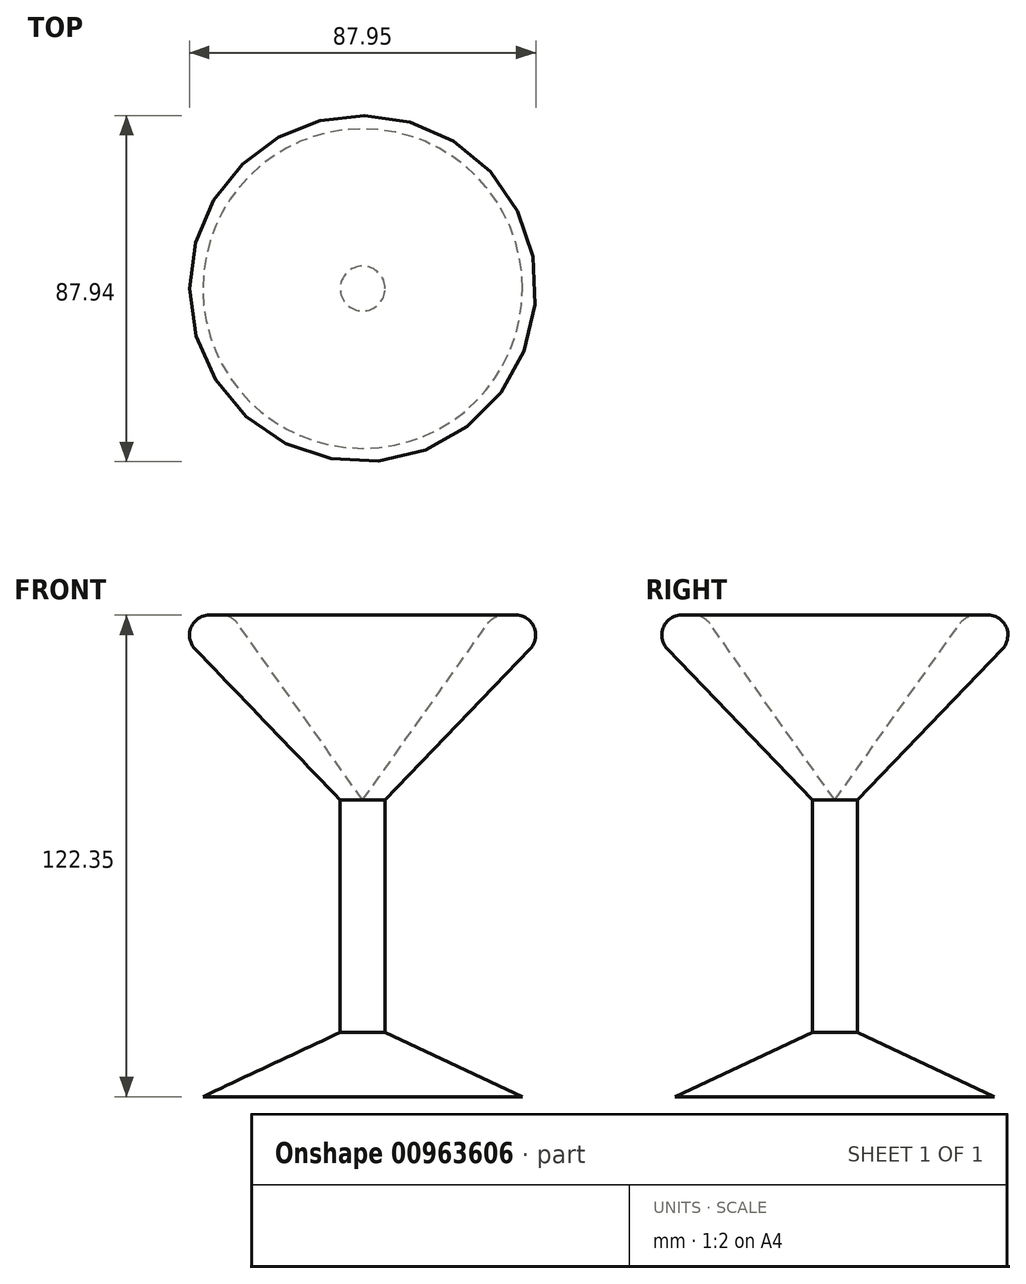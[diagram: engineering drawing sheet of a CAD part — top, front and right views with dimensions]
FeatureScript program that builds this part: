
annotation { "Feature Type Name" : "Feature", "Feature Type Description" : "" }
export const myFeature = defineFeature(function(context is Context, id is Id, definition is map)
    precondition{}
    {
        {
            var Q0;
            Q0=qCreatedBy(makeId("Front.planeOp"),FACE);
            var sketch = newSketch(context, id + "F0", { "sketchPlane" : qUnion([Q0])});
            skLineSegment(sketch, "E0", {"start": v(27.6, 56.5) * mm, "end": v(45.12, 56.5) * mm});
            skLineSegment(sketch, "E1", {"start": v(45.12, 56.5) * mm, "end": v(0, 9.5) * mm});
            skLineSegment(sketch, "E2", {"start": v(0, 9.5) * mm, "end": v(0, -49.5) * mm});
            skLineSegment(sketch, "E3", {"start": v(0, -49.5) * mm, "end": v(34.9, -65.85) * mm});
            skLineSegment(sketch, "E4", {"start": v(34.9, -65.85) * mm, "end": v(-5.7, -65.85) * mm});
            skLineSegment(sketch, "E5", {"start": v(-5.7, -65.85) * mm, "end": v(-5.7, 9.5) * mm});
            skLineSegment(sketch, "E6", {"start": v(-5.7, 9.5) * mm, "end": v(27.6, 56.5) * mm});
            skSolve(sketch);
        }
        {
            var Q0;
            Q0=makeQuery(id+"F0.imprint","IMPRINT",FACE,{"disambiguationData":[TD([[makeQuery(id+"F0.imprint","IMPRINT",EDGE,{"derivedFrom":sQuery(id+"F0.wireOp",EDGE,"E0")}),-1.0]])]});
            var Q1;
            Q1=sQuery(id+"F0.wireOp",EDGE,"E5");
            revolve(context, id + "F1", {"surfaceOperationType" : NewSurfaceOperationType.NEW, "entities" : qUnion([Q0]), "axis" : qUnion([Q1]), "revolveType" : RevolveType.FULL});
        }
        {
            var Q0;
            Q0=makeQuery(id+"F1.opRevolve","SWEPT_EDGE",EDGE,{"disambiguationData":[OSD([sQuery(id+"F0.wireOp",EDGE,"E0"),sQuery(id+"F0.wireOp",EDGE,"E1")])]});
            fillet(context, id + "F2", {"entities" : qUnion([Q0]), "radius" : 5.08 * mm, "tangentPropagation" : true, "allowEdgeOverflow" : false});
        }
        {
            var Q0;
            Q0=makeQuery(id+"F1.opRevolve","SWEPT_EDGE",EDGE,{"disambiguationData":[OSD([sQuery(id+"F0.wireOp",EDGE,"E0"),sQuery(id+"F0.wireOp",EDGE,"E6")])]});
            fillet(context, id + "F3", {"entities" : qUnion([Q0]), "radius" : 5.08 * mm, "tangentPropagation" : true, "allowEdgeOverflow" : false});
        }
    });
